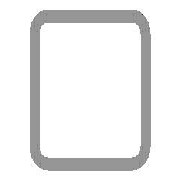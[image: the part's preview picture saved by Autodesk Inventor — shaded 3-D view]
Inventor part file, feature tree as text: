
AUTODESK INVENTOR PART (.ipt)
format: ipt  version: 2022 (Build 260153000, 153)  size: 284,160 bytes
history: native  units: mm (DEFAULTED — no unit token found)
features: plane x7, other x5, sketch x4, extrude x2, boolean_combine x2, sweep x1
ambient origin geometry x8: Origin, YZ Plane, XZ Plane, XY Plane, X Axis, Y Axis, Z Axis, Center Point
bodies: Solid1 (feature_tree), Body (feature_tree), Solid2 (feature_tree), Solid3 (feature_tree)
feature tree (21):
  parser-record x1  (decoder bookkeeping rows leaked as tree rows — omitted from the tree; the rows remain in map.json)
  other  "Driven Length"
  other  "Start Plane"
  other  "End Plane"
  sweep  "Sweep Path"
  other  "Orientation Work Plane"
  plane  "Work Plane5"
  plane  "Work Plane6"
  plane  "Work Plane7"
  extrude  "Extrusion2"  Depth=2.0mm
  boolean_combine  "Combine1"
  plane  "Work Plane8"
  plane  "Work Plane9"
  plane  "Work Plane10"
  extrude  "Extrusion3"  Depth=2899.411255mm
  boolean_combine  "Combine2"
  sketch  "Sketch3"  dims[d7=4.0mm d9=40.0mm]
  plane  "Work Plane3"
  sketch  "Sketch4"  dims[d11=40.0mm d12=2.0mm]
  sketch  "Sketch5"  dims[d13=-0.0mm d14=2899.411255mm]
  sketch  "Sketch6"  dims[d15=20.0mm d16=20.0mm d17=90.0deg d18=2899.411255mm d19=0.0mm d20=0.0mm d21=0.12mm d22=0.0mm d23=0.12mm d24=0.0mm]
